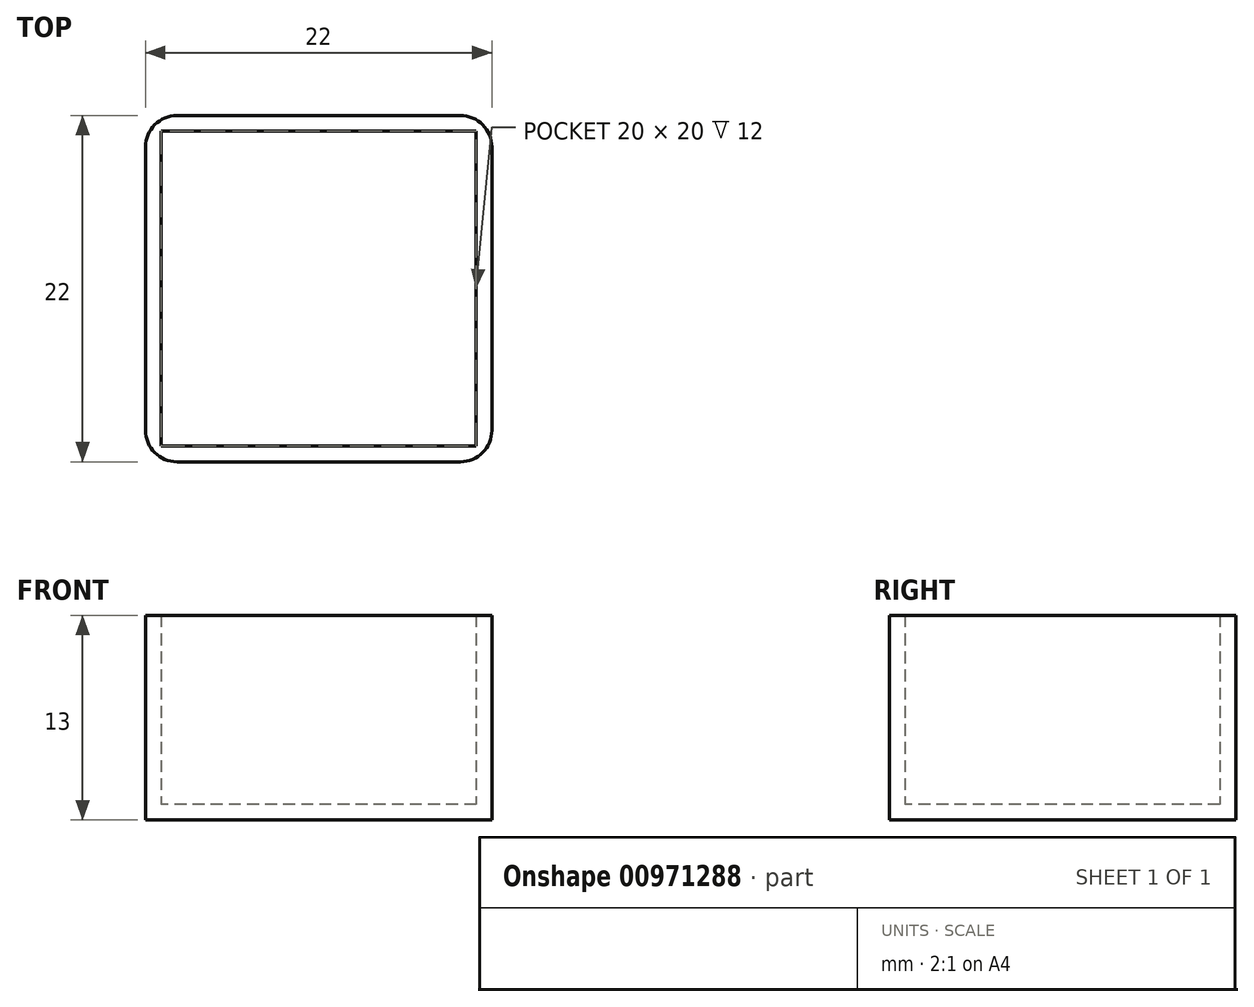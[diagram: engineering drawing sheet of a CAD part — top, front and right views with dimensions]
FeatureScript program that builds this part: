
annotation { "Feature Type Name" : "Feature", "Feature Type Description" : "" }
export const myFeature = defineFeature(function(context is Context, id is Id, definition is map)
    precondition{}
    {
        {
            var Q0;
            Q0=qCreatedBy(makeId("Top.planeOp"),FACE);
            var sketch = newSketch(context, id + "F0", { "sketchPlane" : qUnion([Q0])});
            skLineSegment(sketch, "E0.bottom", {"start": v(10, 10) * mm, "end": v(-10, 10) * mm});
            skLineSegment(sketch, "E0.top", {"start": v(10, -10) * mm, "end": v(-10, -10) * mm});
            skLineSegment(sketch, "E0.left", {"start": v(10, 10) * mm, "end": v(10, -10) * mm});
            skLineSegment(sketch, "E0.right", {"start": v(-10, 10) * mm, "end": v(-10, -10) * mm});
            skPoint(sketch, "E0.middle", {"position": v(0, 0) * mm});
            skLineSegment(sketch, "E1.bottom", {"start": v(11, 11) * mm, "end": v(-11, 11) * mm});
            skLineSegment(sketch, "E1.top", {"start": v(11, -11) * mm, "end": v(-11, -11) * mm});
            skLineSegment(sketch, "E1.left", {"start": v(11, 11) * mm, "end": v(11, -11) * mm});
            skLineSegment(sketch, "E1.right", {"start": v(-11, 11) * mm, "end": v(-11, -11) * mm});
            skSolve(sketch);
        }
        {
            var Q0;
            Q0=makeQuery(id+"F0.imprint","IMPRINT",FACE,{"disambiguationData":[TD([[makeQuery(id+"F0.imprint","IMPRINT",EDGE,{"derivedFrom":sQuery(id+"F0.wireOp",EDGE,"E0.bottom")}),-1.0]])]});
            extrude(context, id + "F1", {"entities" : qUnion([Q0]), "depth" : 12 * mm, "offsetDistance" : 25 * mm});
        }
        {
            var Q0;
            Q0=makeQuery(id+"F0.imprint","IMPRINT",FACE,{"disambiguationData":[TD([[makeQuery(id+"F0.imprint","IMPRINT",EDGE,{"derivedFrom":sQuery(id+"F0.wireOp",EDGE,"E0.bottom")}),1.0]])]});
            var Q1;
            Q1=makeQuery(id+"F0.imprint","IMPRINT",FACE,{"disambiguationData":[TD([[makeQuery(id+"F0.imprint","IMPRINT",EDGE,{"derivedFrom":sQuery(id+"F0.wireOp",EDGE,"E0.bottom")}),-1.0]])]});
            extrude(context, id + "F2", {"entities" : qUnion([Q0, Q1]), "operationType" : NewBodyOperationType.ADD, "oppositeDirection" : true, "depth" : 1 * mm, "offsetDistance" : 25 * mm});
        }
        {
            var Q0;
            {var subQ0=sQuery(id+"F0.wireOp",EDGE,"E1.right");var subQ1=sQuery(id+"F0.wireOp",EDGE,"E1.bottom");Q0=makeQuery(id+"F2.boolean.opBoolean","MERGE",EDGE,{"derivedFrom":[makeQuery(id+"F1.opExtrude","SWEPT_EDGE",EDGE,{"disambiguationData":[OSD([subQ1,subQ0])]}),makeQuery(id+"F2.opExtrude","SWEPT_EDGE",EDGE,{"disambiguationData":[OSD([subQ1,subQ0])]})]});}
            var Q1;
            {var subQ0=sQuery(id+"F0.wireOp",EDGE,"E1.right");var subQ1=sQuery(id+"F0.wireOp",EDGE,"E1.top");Q1=makeQuery(id+"F2.boolean.opBoolean","MERGE",EDGE,{"derivedFrom":[makeQuery(id+"F1.opExtrude","SWEPT_EDGE",EDGE,{"disambiguationData":[OSD([subQ1,subQ0])]}),makeQuery(id+"F2.opExtrude","SWEPT_EDGE",EDGE,{"disambiguationData":[OSD([subQ1,subQ0])]})]});}
            var Q2;
            {var subQ0=sQuery(id+"F0.wireOp",EDGE,"E1.left");var subQ1=sQuery(id+"F0.wireOp",EDGE,"E1.bottom");Q2=makeQuery(id+"F2.boolean.opBoolean","MERGE",EDGE,{"derivedFrom":[makeQuery(id+"F1.opExtrude","SWEPT_EDGE",EDGE,{"disambiguationData":[OSD([subQ1,subQ0])]}),makeQuery(id+"F2.opExtrude","SWEPT_EDGE",EDGE,{"disambiguationData":[OSD([subQ1,subQ0])]})]});}
            var Q3;
            {var subQ0=sQuery(id+"F0.wireOp",EDGE,"E1.left");var subQ1=sQuery(id+"F0.wireOp",EDGE,"E1.top");Q3=makeQuery(id+"F2.boolean.opBoolean","MERGE",EDGE,{"derivedFrom":[makeQuery(id+"F1.opExtrude","SWEPT_EDGE",EDGE,{"disambiguationData":[OSD([subQ1,subQ0])]}),makeQuery(id+"F2.opExtrude","SWEPT_EDGE",EDGE,{"disambiguationData":[OSD([subQ1,subQ0])]})]});}
            fillet(context, id + "F3", {"entities" : qUnion([Q0, Q1, Q2, Q3]), "radius" : 2 * mm, "tangentPropagation" : true, "allowEdgeOverflow" : false});
        }
    });
